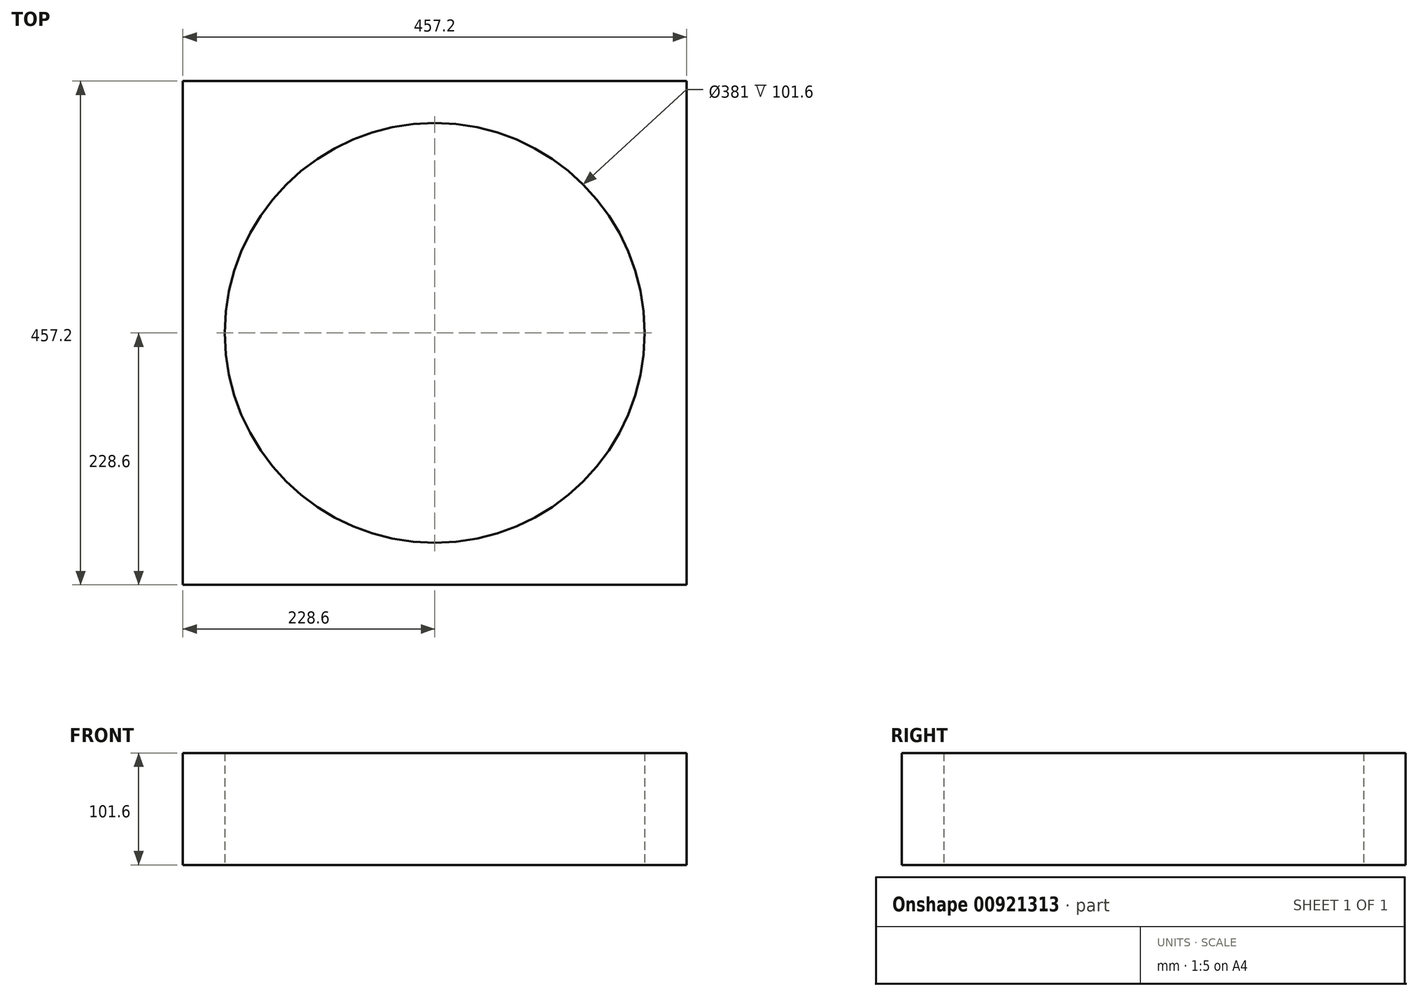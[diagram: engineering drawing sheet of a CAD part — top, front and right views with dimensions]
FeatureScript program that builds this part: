
annotation { "Feature Type Name" : "Feature", "Feature Type Description" : "" }
export const myFeature = defineFeature(function(context is Context, id is Id, definition is map)
    precondition{}
    {
        {
            var Q0;
            Q0=qCreatedBy(makeId("Top.planeOp"),FACE);
            var sketch = newSketch(context, id + "F0", { "sketchPlane" : qUnion([Q0])});
            skCircle(sketch, "E0", {"center": v(0, 0) * mm, "radius": 190.5 * mm});
            skLineSegment(sketch, "E1.bottom", {"start": v(-228.6, 228.6) * mm, "end": v(228.6, 228.6) * mm});
            skLineSegment(sketch, "E1.top", {"start": v(-228.6, -228.6) * mm, "end": v(228.6, -228.6) * mm});
            skLineSegment(sketch, "E1.left", {"start": v(-228.6, 228.6) * mm, "end": v(-228.6, -228.6) * mm});
            skLineSegment(sketch, "E1.right", {"start": v(228.6, 228.6) * mm, "end": v(228.6, -228.6) * mm});
            skCircle(sketch, "E2", {"center": v(0, 0) * mm, "radius": 3.97 * mm});
            skSolve(sketch);
        }
        {
            var Q0;
            Q0=makeQuery(id+"F0.imprint","IMPRINT",FACE,{"disambiguationData":[TD([[makeQuery(id+"F0.imprint","IMPRINT",EDGE,{"derivedFrom":sQuery(id+"F0.wireOp",EDGE,"E0")}),-1.0]])]});
            extrude(context, id + "F1", {"entities" : qUnion([Q0]), "depth" : 101.6 * mm, "offsetDistance" : 25.4 * mm});
        }
    });
